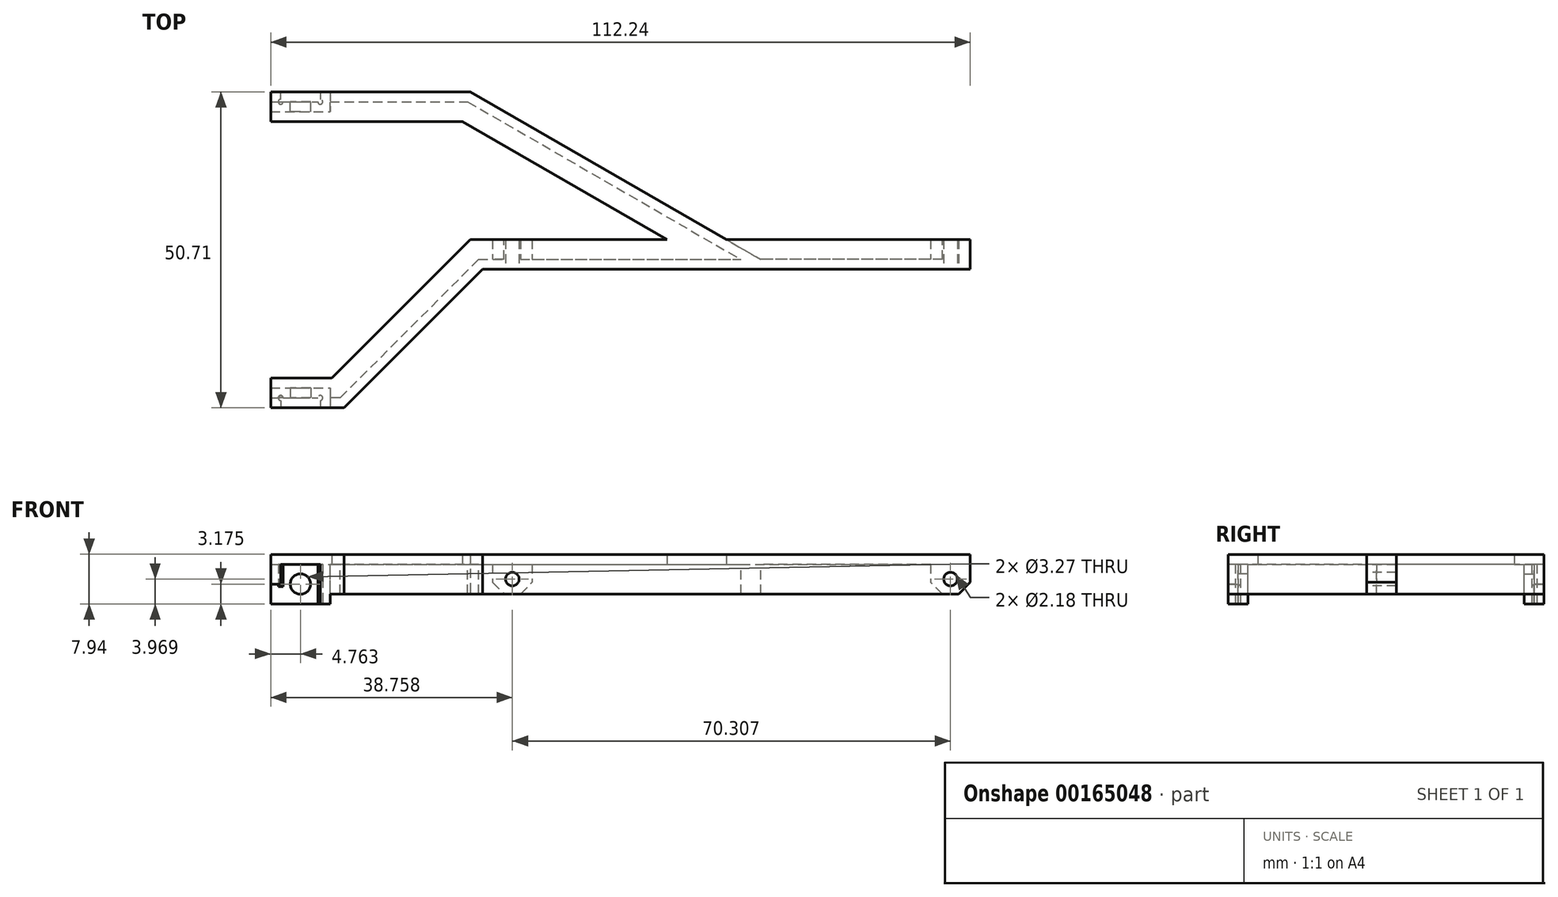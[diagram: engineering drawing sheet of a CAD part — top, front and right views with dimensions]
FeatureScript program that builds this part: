
annotation { "Feature Type Name" : "Feature", "Feature Type Description" : "" }
export const myFeature = defineFeature(function(context is Context, id is Id, definition is map)
    precondition{}
    {
        {
            var Q0;
            Q0=qCreatedBy(makeId("Top.planeOp"),FACE);
            var sketch = newSketch(context, id + "F0", { "sketchPlane" : qUnion([Q0])});
            skLineSegment(sketch, "E0", {"start": v(-127, 22.22) * mm, "end": v(-87.88, 22.22) * mm});
            skLineSegment(sketch, "E1", {"start": v(-46.78, 22.23) * mm, "end": v(-24.56, 0) * mm});
            skLineSegment(sketch, "E2", {"start": v(-24.56, 0) * mm, "end": v(24.56, 0) * mm});
            skLineSegment(sketch, "E3", {"start": v(24.56, 0) * mm, "end": v(46.78, 22.23) * mm});
            skLineSegment(sketch, "E4", {"start": v(87.88, 22.23) * mm, "end": v(127, 22.23) * mm});
            skLineSegment(sketch, "E5", {"start": v(-127, 22.23) * mm, "end": v(-127, 17.46) * mm});
            skLineSegment(sketch, "E6", {"start": v(-127, 17.46) * mm, "end": v(-48.76, 17.46) * mm});
            skLineSegment(sketch, "E7", {"start": v(-48.76, 17.46) * mm, "end": v(-26.53, -4.76) * mm});
            skLineSegment(sketch, "E8", {"start": v(-26.53, -4.76) * mm, "end": v(26.53, -4.76) * mm});
            skLineSegment(sketch, "E9", {"start": v(26.53, -4.76) * mm, "end": v(48.76, 17.46) * mm});
            skLineSegment(sketch, "E10", {"start": v(48.76, 17.46) * mm, "end": v(127, 17.46) * mm});
            skLineSegment(sketch, "E11", {"start": v(127, 17.46) * mm, "end": v(127, 22.23) * mm});
            skLineSegment(sketch, "E12", {"start": v(-35.67, 11.11) * mm, "end": v(-39.04, 7.74) * mm, "construction": true});
            skLineSegment(sketch, "E13", {"start": v(0, 0) * mm, "end": v(0, -4.76) * mm, "construction": true});
            skLineSegment(sketch, "E14", {"start": v(35.67, 11.11) * mm, "end": v(39.04, 7.74) * mm, "construction": true});
            skLineSegment(sketch, "E15", {"start": v(-87.88, 17.46) * mm, "end": v(-87.88, 22.23) * mm, "construction": true});
            skLineSegment(sketch, "E16", {"start": v(87.88, 17.46) * mm, "end": v(87.88, 22.23) * mm, "construction": true});
            skLineSegment(sketch, "E17", {"start": v(-87.88, 22.23) * mm, "end": v(-46.78, 45.95) * mm});
            skLineSegment(sketch, "E18", {"start": v(-78.35, 22.23) * mm, "end": v(-45.5, 41.19) * mm});
            skLineSegment(sketch, "E19", {"start": v(-45.5, 41.19) * mm, "end": v(45.5, 41.19) * mm});
            skLineSegment(sketch, "E20", {"start": v(-46.78, 45.95) * mm, "end": v(46.78, 45.95) * mm});
            skLineSegment(sketch, "E21", {"start": v(-78.35, 22.22) * mm, "end": v(-46.78, 22.22) * mm});
            skLineSegment(sketch, "E22", {"start": v(45.5, 41.19) * mm, "end": v(78.35, 22.22) * mm});
            skLineSegment(sketch, "E23", {"start": v(46.78, 45.95) * mm, "end": v(87.88, 22.22) * mm});
            skLineSegment(sketch, "E24", {"start": v(46.78, 22.23) * mm, "end": v(78.35, 22.23) * mm});
            skLineSegment(sketch, "E25", {"start": v(0, 0) * mm, "end": v(0, 41.19) * mm, "construction": true});
            skLineSegment(sketch, "E26", {"start": v(0, 41.19) * mm, "end": v(0, 45.95) * mm, "construction": true});
            skLineSegment(sketch, "E27", {"start": v(-61.93, 31.7) * mm, "end": v(-64.31, 35.83) * mm, "construction": true});
            skLineSegment(sketch, "E28", {"start": v(61.93, 31.7) * mm, "end": v(64.31, 35.83) * mm, "construction": true});
            skLineSegment(sketch, "E29", {"start": v(-46.78, 22.23) * mm, "end": v(0, 22.23) * mm, "construction": true});
            skLineSegment(sketch, "E30", {"start": v(0, 22.23) * mm, "end": v(46.78, 22.23) * mm, "construction": true});
            skSolve(sketch);
        }
        {
            var Q0;
            Q0=qSketchRegion(id+"F0",true);
            extrude(context, id + "F1", {"entities" : qUnion([Q0]), "depth" : 1.59 * mm});
        }
        {
            var Q0;
            Q0=makeQuery(id+"F1.opExtrude","CAP_FACE",FACE,{"disambiguationData":[OSD([sQuery(id+"F0.wireOp",EDGE,"E0"),sQuery(id+"F0.wireOp",EDGE,"E1"),sQuery(id+"F0.wireOp",EDGE,"E2"),sQuery(id+"F0.wireOp",EDGE,"E3"),sQuery(id+"F0.wireOp",EDGE,"E4"),sQuery(id+"F0.wireOp",EDGE,"E5"),sQuery(id+"F0.wireOp",EDGE,"E6"),sQuery(id+"F0.wireOp",EDGE,"E7"),sQuery(id+"F0.wireOp",EDGE,"E8"),sQuery(id+"F0.wireOp",EDGE,"E9"),sQuery(id+"F0.wireOp",EDGE,"E10"),sQuery(id+"F0.wireOp",EDGE,"E11"),sQuery(id+"F0.wireOp",EDGE,"E17"),sQuery(id+"F0.wireOp",EDGE,"E18"),sQuery(id+"F0.wireOp",EDGE,"E19"),sQuery(id+"F0.wireOp",EDGE,"E20"),sQuery(id+"F0.wireOp",EDGE,"E21"),sQuery(id+"F0.wireOp",EDGE,"E22"),sQuery(id+"F0.wireOp",EDGE,"E23"),sQuery(id+"F0.wireOp",EDGE,"E24")])],"isStart":true});
            var sketch = newSketch(context, id + "F2", { "sketchPlane" : qUnion([Q0])});
            skLineSegment(sketch, "E31.bottom", {"start": v(-127, -17.46) * mm, "end": v(-48.76, -17.46) * mm});
            skLineSegment(sketch, "E31.top", {"start": v(-127, -19.05) * mm, "end": v(-93.38, -19.05) * mm});
            skLineSegment(sketch, "E31.left", {"start": v(-127, -19.05) * mm, "end": v(-127, -17.46) * mm});
            skLineSegment(sketch, "E32", {"start": v(-48.76, -17.46) * mm, "end": v(-26.53, 4.76) * mm});
            skLineSegment(sketch, "E33", {"start": v(-26.53, 4.76) * mm, "end": v(26.53, 4.76) * mm});
            skLineSegment(sketch, "E34", {"start": v(26.53, 4.76) * mm, "end": v(48.76, -17.46) * mm});
            skLineSegment(sketch, "E35", {"start": v(48.76, -17.46) * mm, "end": v(127, -17.46) * mm});
            skLineSegment(sketch, "E36", {"start": v(127, -19.05) * mm, "end": v(127, -17.46) * mm});
            skLineSegment(sketch, "E37", {"start": v(127, -19.05) * mm, "end": v(93.38, -19.05) * mm});
            skLineSegment(sketch, "E38", {"start": v(-25.87, 3.18) * mm, "end": v(-48.1, -19.05) * mm});
            skLineSegment(sketch, "E39", {"start": v(-36.52, -7.47) * mm, "end": v(-37.64, -6.35) * mm, "construction": true});
            skLineSegment(sketch, "E40", {"start": v(36.52, -7.47) * mm, "end": v(37.64, -6.35) * mm, "construction": true});
            skLineSegment(sketch, "E41", {"start": v(0, 4.76) * mm, "end": v(0, 3.17) * mm, "construction": true});
            skLineSegment(sketch, "E42", {"start": v(-25.87, 3.17) * mm, "end": v(-4.29, 3.17) * mm});
            skLineSegment(sketch, "E43.top", {"start": v(-4.29, 1.59) * mm, "end": v(24.29, 1.59) * mm});
            skLineSegment(sketch, "E43.left", {"start": v(-4.29, 1.59) * mm, "end": v(-4.29, 3.18) * mm});
            skLineSegment(sketch, "E43.right", {"start": v(24.29, 1.59) * mm, "end": v(24.29, 3.18) * mm});
            skLineSegment(sketch, "E44", {"start": v(-46.78, -45.95) * mm, "end": v(-93.38, -19.05) * mm});
            skLineSegment(sketch, "E45", {"start": v(-46.78, -45.95) * mm, "end": v(46.78, -45.95) * mm});
            skLineSegment(sketch, "E46", {"start": v(46.78, -45.95) * mm, "end": v(93.38, -19.05) * mm});
            skLineSegment(sketch, "E47", {"start": v(-66.54, -32.71) * mm, "end": v(-67.33, -34.09) * mm, "construction": true});
            skLineSegment(sketch, "E48", {"start": v(0, -44.36) * mm, "end": v(0, -45.95) * mm, "construction": true});
            skLineSegment(sketch, "E49", {"start": v(66.54, -32.71) * mm, "end": v(67.33, -34.09) * mm, "construction": true});
            skLineSegment(sketch, "E50", {"start": v(-90.2, -19.05) * mm, "end": v(-46.36, -44.36) * mm});
            skLineSegment(sketch, "E51", {"start": v(46.36, -44.36) * mm, "end": v(90.2, -19.05) * mm});
            skLineSegment(sketch, "E52", {"start": v(-48.1, -19.05) * mm, "end": v(-90.2, -19.05) * mm});
            skLineSegment(sketch, "E53", {"start": v(48.1, -19.05) * mm, "end": v(90.2, -19.05) * mm});
            skLineSegment(sketch, "E54.bottom", {"start": v(-4.29, -44.36) * mm, "end": v(24.29, -44.36) * mm, "construction": true});
            skLineSegment(sketch, "E54.top", {"start": v(-4.29, -42.78) * mm, "end": v(24.29, -42.78) * mm});
            skLineSegment(sketch, "E54.left", {"start": v(-4.29, -42.78) * mm, "end": v(-4.29, -44.36) * mm});
            skLineSegment(sketch, "E54.right", {"start": v(24.29, -42.78) * mm, "end": v(24.29, -44.36) * mm});
            skLineSegment(sketch, "E55", {"start": v(-4.29, -44.36) * mm, "end": v(-46.36, -44.36) * mm});
            skLineSegment(sketch, "E56", {"start": v(24.29, -44.36) * mm, "end": v(46.36, -44.36) * mm});
            skLineSegment(sketch, "E57", {"start": v(24.29, 3.17) * mm, "end": v(-4.29, 3.17) * mm, "construction": true});
            skLineSegment(sketch, "E58", {"start": v(48.1, -19.05) * mm, "end": v(25.87, 3.18) * mm});
            skLineSegment(sketch, "E59", {"start": v(25.87, 3.18) * mm, "end": v(24.29, 3.18) * mm});
            skSolve(sketch);
        }
        {
            var Q0;
            Q0=makeQuery(id+"F2.imprint","IMPRINT",FACE,{"disambiguationData":[TD([[makeQuery(id+"F2.imprint","IMPRINT",EDGE,{"derivedFrom":sQuery(id+"F2.wireOp",EDGE,"E31.bottom")}),1.0]])]});
            var Q1;
            Q1=makeQuery(id+"F2.imprint","IMPRINT",FACE,{"disambiguationData":[TD([[makeQuery(id+"F2.imprint","IMPRINT",EDGE,{"derivedFrom":sQuery(id+"F2.wireOp",EDGE,"E31.bottom")}),-1.0]])]});
            extrude(context, id + "F3", {"entities" : qUnion([Q0, Q1]), "operationType" : NewBodyOperationType.ADD, "depth" : 4.76 * mm});
        }
        {
            var Q0;
            Q0=makeQuery(id+"F3.opExtrude","SWEPT_FACE",FACE,{"disambiguationData":[OSD([sQuery(id+"F2.wireOp",EDGE,"E31.top")])]});
            var sketch = newSketch(context, id + "F4", { "sketchPlane" : qUnion([Q0])});
            skLineSegment(sketch, "E60.bottom", {"start": v(-50.34, -4.76) * mm, "end": v(-56.7, -4.76) * mm});
            skLineSegment(sketch, "E60.top", {"start": v(-50.34, 1.59) * mm, "end": v(-56.7, 1.59) * mm});
            skLineSegment(sketch, "E60.left", {"start": v(-50.34, 1.59) * mm, "end": v(-50.34, -4.76) * mm});
            skLineSegment(sketch, "E60.right", {"start": v(-56.7, 1.59) * mm, "end": v(-56.7, -4.76) * mm});
            skLineSegment(sketch, "E61", {"start": v(-50.34, -1.59) * mm, "end": v(-48.76, -1.59) * mm, "construction": true});
            skLineSegment(sketch, "E62.bottom", {"start": v(-127, -4.76) * mm, "end": v(-120.65, -4.76) * mm});
            skLineSegment(sketch, "E62.top", {"start": v(-127, 1.59) * mm, "end": v(-120.65, 1.59) * mm});
            skLineSegment(sketch, "E62.left", {"start": v(-127, 1.59) * mm, "end": v(-127, -4.76) * mm});
            skLineSegment(sketch, "E62.right", {"start": v(-120.65, 1.59) * mm, "end": v(-120.65, -4.76) * mm});
            skLineSegment(sketch, "E63.bottom", {"start": v(127, -4.76) * mm, "end": v(122.24, -4.76) * mm});
            skLineSegment(sketch, "E63.top", {"start": v(127, 0) * mm, "end": v(122.24, 0) * mm});
            skLineSegment(sketch, "E63.left", {"start": v(127, 0) * mm, "end": v(127, -4.76) * mm});
            skLineSegment(sketch, "E63.right", {"start": v(122.24, 0) * mm, "end": v(122.24, -4.76) * mm});
            skLineSegment(sketch, "E64.bottom", {"start": v(53.52, -4.76) * mm, "end": v(58.28, -4.76) * mm});
            skLineSegment(sketch, "E64.top", {"start": v(53.52, 0) * mm, "end": v(58.28, 0) * mm});
            skLineSegment(sketch, "E64.left", {"start": v(53.52, 0) * mm, "end": v(53.52, -4.76) * mm});
            skLineSegment(sketch, "E64.right", {"start": v(58.28, 0) * mm, "end": v(58.28, -4.76) * mm});
            skLineSegment(sketch, "E65", {"start": v(122.24, -2.38) * mm, "end": v(58.28, -2.38) * mm, "construction": true});
            skLineSegment(sketch, "E66", {"start": v(-56.7, -1.59) * mm, "end": v(-120.65, -1.59) * mm, "construction": true});
            skSolve(sketch);
        }
        {
            var Q0;
            Q0=qSketchRegion(id+"F4",true);
            var Q1;
            Q1=makeQuery(id+"F1.opExtrude","SWEPT_FACE",FACE,{"disambiguationData":[OSD([sQuery(id+"F0.wireOp",EDGE,"E0")])]});
            extrude(context, id + "F5", {"entities" : qUnion([Q0]), "operationType" : NewBodyOperationType.ADD, "endBound" : BoundingType.UP_TO_SURFACE, "endBoundEntityFace" : qUnion([Q1]), "depth" : 25.4 * mm});
        }
        {
            var Q0;
            Q0=makeQuery(id+"F5.boolean.opBoolean","MERGE",EDGE,{"derivedFrom":[makeQuery(id+"F3.opExtrude","CAP_EDGE",EDGE,{"disambiguationData":[OSD([sQuery(id+"F2.wireOp",EDGE,"E31.left")])],"isStart":false}),makeQuery(id+"F5.opExtrude","SWEPT_EDGE",EDGE,{"disambiguationData":[OSD([sQuery(id+"F4.wireOp",EDGE,"E63.bottom"),sQuery(id+"F4.wireOp",EDGE,"E63.left")])]})]});
            var Q1;
            Q1=makeQuery(id+"F5.opExtrude","SWEPT_EDGE",EDGE,{"disambiguationData":[OSD([sQuery(id+"F2.wireOp",EDGE,"E31.top"),sQuery(id+"F4.wireOp",EDGE,"E63.bottom"),sQuery(id+"F4.wireOp",EDGE,"E63.right")])]});
            var Q2;
            Q2=makeQuery(id+"F5.opExtrude","SWEPT_EDGE",EDGE,{"disambiguationData":[OSD([sQuery(id+"F2.wireOp",EDGE,"E31.top"),sQuery(id+"F4.wireOp",EDGE,"E64.bottom"),sQuery(id+"F4.wireOp",EDGE,"E64.right")])]});
            var Q3;
            Q3=makeQuery(id+"F5.opExtrude","SWEPT_EDGE",EDGE,{"disambiguationData":[OSD([sQuery(id+"F2.wireOp",EDGE,"E31.top"),sQuery(id+"F4.wireOp",EDGE,"E64.bottom"),sQuery(id+"F4.wireOp",EDGE,"E64.left")])]});
            var Q4;
            Q4=makeQuery(id+"F5.opExtrude","SWEPT_EDGE",EDGE,{"disambiguationData":[OSD([sQuery(id+"F4.wireOp",EDGE,"E60.bottom"),sQuery(id+"F4.wireOp",EDGE,"E60.left")])]});
            var Q5;
            Q5=makeQuery(id+"F5.opExtrude","SWEPT_EDGE",EDGE,{"disambiguationData":[OSD([sQuery(id+"F4.wireOp",EDGE,"E60.bottom"),sQuery(id+"F4.wireOp",EDGE,"E60.right")])]});
            var Q6;
            Q6=makeQuery(id+"F5.opExtrude","SWEPT_EDGE",EDGE,{"disambiguationData":[OSD([sQuery(id+"F4.wireOp",EDGE,"E62.bottom"),sQuery(id+"F4.wireOp",EDGE,"E62.right")])]});
            var Q7;
            Q7=makeQuery(id+"F5.boolean.opBoolean","MERGE",EDGE,{"derivedFrom":[makeQuery(id+"F3.opExtrude","CAP_EDGE",EDGE,{"disambiguationData":[OSD([sQuery(id+"F2.wireOp",EDGE,"E36")])],"isStart":false}),makeQuery(id+"F5.opExtrude","SWEPT_EDGE",EDGE,{"disambiguationData":[OSD([sQuery(id+"F4.wireOp",EDGE,"E62.bottom"),sQuery(id+"F4.wireOp",EDGE,"E62.left")])]})]});
            chamfer(context, id + "F6", {"entities" : qUnion([Q0, Q1, Q2, Q3, Q4, Q5, Q6, Q7]), "width" : 1.86 * mm, "tangentPropagation" : true});
        }
        {
            var Q0;
            Q0=makeQuery(id+"F5.boolean.opBoolean","MERGE",FACE,{"derivedFrom":[makeQuery(id+"F3.opExtrude","CAP_FACE",FACE,{"disambiguationData":[OSD([sQuery(id+"F2.wireOp",EDGE,"E31.bottom"),sQuery(id+"F2.wireOp",EDGE,"E31.top"),sQuery(id+"F2.wireOp",EDGE,"E31.left"),sQuery(id+"F2.wireOp",EDGE,"E32"),sQuery(id+"F2.wireOp",EDGE,"E33"),sQuery(id+"F2.wireOp",EDGE,"E34"),sQuery(id+"F2.wireOp",EDGE,"E35"),sQuery(id+"F2.wireOp",EDGE,"E36"),sQuery(id+"F2.wireOp",EDGE,"E37"),sQuery(id+"F2.wireOp",EDGE,"XaXFcP98-jHVc-UIB6-hOLf-KzhYTJMkncuN"),sQuery(id+"F2.wireOp",EDGE,"E38"),sQuery(id+"F2.wireOp",EDGE,"E42"),sQuery(id+"F2.wireOp",EDGE,"r7zNDvTV-qKGN-hqvY-1zE9-Y1A1LRN73BV9"),sQuery(id+"F2.wireOp",EDGE,"E43.top"),sQuery(id+"F2.wireOp",EDGE,"E43.left"),sQuery(id+"F2.wireOp",EDGE,"E43.right")])],"isStart":false}),makeQuery(id+"F5.opExtrude","SWEPT_FACE",FACE,{"disambiguationData":[OSD([sQuery(id+"F4.wireOp",EDGE,"E60.bottom")])]}),makeQuery(id+"F5.opExtrude","SWEPT_FACE",FACE,{"disambiguationData":[OSD([sQuery(id+"F4.wireOp",EDGE,"E62.bottom")])]}),makeQuery(id+"F5.opExtrude","SWEPT_FACE",FACE,{"disambiguationData":[OSD([sQuery(id+"F4.wireOp",EDGE,"E63.bottom")])]}),makeQuery(id+"F5.opExtrude","SWEPT_FACE",FACE,{"disambiguationData":[OSD([sQuery(id+"F4.wireOp",EDGE,"E64.bottom")])]})]});
            var sketch = newSketch(context, id + "F7", { "sketchPlane" : qUnion([Q0])});
            skLineSegment(sketch, "E67.bottom", {"start": v(-4.29, 1.59) * mm, "end": v(24.29, 1.59) * mm});
            skLineSegment(sketch, "E67.top", {"start": v(-4.29, 4.76) * mm, "end": v(24.29, 4.76) * mm});
            skLineSegment(sketch, "E67.left", {"start": v(-4.29, 4.76) * mm, "end": v(-4.29, 1.59) * mm});
            skLineSegment(sketch, "E67.right", {"start": v(24.29, 4.76) * mm, "end": v(24.29, 1.59) * mm});
            skLineSegment(sketch, "E68.bottom", {"start": v(-4.29, -42.78) * mm, "end": v(24.29, -42.78) * mm});
            skLineSegment(sketch, "E68.top", {"start": v(-4.29, -45.95) * mm, "end": v(24.29, -45.95) * mm});
            skLineSegment(sketch, "E68.left", {"start": v(-4.29, -45.95) * mm, "end": v(-4.29, -42.78) * mm});
            skLineSegment(sketch, "E68.right", {"start": v(24.29, -45.95) * mm, "end": v(24.29, -42.78) * mm});
            skSolve(sketch);
        }
        {
            var Q0;
            Q0=qSketchRegion(id+"F7",true);
            extrude(context, id + "F8", {"entities" : qUnion([Q0]), "operationType" : NewBodyOperationType.ADD, "depth" : 1.59 * mm});
        }
        {
            var Q0;
            Q0=makeQuery(id+"F8.opExtrude","CAP_FACE",FACE,{"disambiguationData":[OSD([sQuery(id+"F7.wireOp",EDGE,"E68.bottom"),sQuery(id+"F7.wireOp",EDGE,"E68.top"),sQuery(id+"F7.wireOp",EDGE,"E68.left"),sQuery(id+"F7.wireOp",EDGE,"E68.right")])],"isStart":false});
            var sketch = newSketch(context, id + "F9", { "sketchPlane" : qUnion([Q0])});
            skLineSegment(sketch, "E69.bottom", {"start": v(16.35, 4.76) * mm, "end": v(22.7, 4.76) * mm});
            skLineSegment(sketch, "E69.top", {"start": v(16.35, 3.17) * mm, "end": v(22.7, 3.17) * mm});
            skLineSegment(sketch, "E69.left", {"start": v(16.35, 3.17) * mm, "end": v(16.35, 4.76) * mm});
            skLineSegment(sketch, "E69.right", {"start": v(22.7, 3.17) * mm, "end": v(22.7, 4.76) * mm});
            skLineSegment(sketch, "E70.bottom", {"start": v(22.7, 3.17) * mm, "end": v(24.29, 3.17) * mm, "construction": true});
            skLineSegment(sketch, "E70.top", {"start": v(22.7, 1.59) * mm, "end": v(24.29, 1.59) * mm, "construction": true});
            skLineSegment(sketch, "E70.left", {"start": v(22.7, 1.59) * mm, "end": v(22.7, 3.17) * mm, "construction": true});
            skLineSegment(sketch, "E70.right", {"start": v(24.29, 1.59) * mm, "end": v(24.29, 3.17) * mm, "construction": true});
            skLineSegment(sketch, "E71.bottom", {"start": v(24.29, -44.36) * mm, "end": v(22.7, -44.36) * mm, "construction": true});
            skLineSegment(sketch, "E71.top", {"start": v(24.29, -42.78) * mm, "end": v(22.7, -42.78) * mm, "construction": true});
            skLineSegment(sketch, "E71.left", {"start": v(24.29, -42.78) * mm, "end": v(24.29, -44.36) * mm, "construction": true});
            skLineSegment(sketch, "E71.right", {"start": v(22.7, -42.78) * mm, "end": v(22.7, -44.36) * mm, "construction": true});
            skLineSegment(sketch, "E72.bottom", {"start": v(16.35, -44.36) * mm, "end": v(22.7, -44.36) * mm});
            skLineSegment(sketch, "E72.top", {"start": v(16.35, -45.95) * mm, "end": v(22.7, -45.95) * mm});
            skLineSegment(sketch, "E72.left", {"start": v(16.35, -45.95) * mm, "end": v(16.35, -44.36) * mm});
            skLineSegment(sketch, "E72.right", {"start": v(22.7, -45.95) * mm, "end": v(22.7, -44.36) * mm});
            skSolve(sketch);
        }
        {
            var Q0;
            Q0=qSketchRegion(id+"F9",true);
            var Q1;
            {var subQ2=sQuery(id+"F0.wireOp",EDGE,"E21");var subQ7=sQuery(id+"F0.wireOp",EDGE,"E24");var subQ10=sQuery(id+"F0.wireOp",EDGE,"E1");var subQ11=makeQuery(id+"F1.opExtrude","SWEPT_FACE",FACE,{"disambiguationData":[OSD([subQ10])]});var subQ14=sQuery(id+"F0.wireOp",EDGE,"E2");var subQ17=sQuery(id+"F0.wireOp",EDGE,"E3");var subQ19=sQuery(id+"F0.wireOp",EDGE,"E0");var subQ22=sQuery(id+"F0.wireOp",EDGE,"E18");var subQ23=sQuery(id+"F0.wireOp",EDGE,"E19");var subQ24=sQuery(id+"F0.wireOp",EDGE,"E22");Q1=makeQuery(id+"F5.boolean.opBoolean","SPLIT",FACE,{"disambiguationData":[TD([subQ11])],"derivedFrom":makeQuery(id+"F3.boolean.opBoolean","SPLIT",FACE,{"disambiguationData":[TD([subQ11])],"derivedFrom":makeQuery(id+"F1.opExtrude","CAP_FACE",FACE,{"disambiguationData":[OSD([subQ19,subQ10,subQ14,subQ17,sQuery(id+"F0.wireOp",EDGE,"E4"),sQuery(id+"F0.wireOp",EDGE,"E5"),sQuery(id+"F0.wireOp",EDGE,"E6"),sQuery(id+"F0.wireOp",EDGE,"E7"),sQuery(id+"F0.wireOp",EDGE,"E8"),sQuery(id+"F0.wireOp",EDGE,"E9"),sQuery(id+"F0.wireOp",EDGE,"E10"),sQuery(id+"F0.wireOp",EDGE,"E11"),sQuery(id+"F0.wireOp",EDGE,"E17"),subQ22,subQ23,sQuery(id+"F0.wireOp",EDGE,"E20"),subQ2,subQ24,sQuery(id+"F0.wireOp",EDGE,"E23"),subQ7])],"isStart":true})})});}
            extrude(context, id + "F10", {"entities" : qUnion([Q0]), "operationType" : NewBodyOperationType.REMOVE, "endBound" : BoundingType.UP_TO_SURFACE, "oppositeDirection" : true, "endBoundEntityFace" : qUnion([Q1]), "depth" : 25.4 * mm});
        }
        {
            var Q0;
            Q0=makeQuery(id+"F10.boolean.opBoolean","COPY",FACE,{"derivedFrom":makeQuery(id+"F10.opExtrude","SWEPT_FACE",FACE,{"disambiguationData":[OSD([sQuery(id+"F9.wireOp",EDGE,"E69.top")])]})});
            var sketch = newSketch(context, id + "F11", { "sketchPlane" : qUnion([Q0])});
            skLineSegment(sketch, "E73", {"start": v(123.83, 0) * mm, "end": v(123.83, -4.76) * mm, "construction": true});
            skLineSegment(sketch, "E74", {"start": v(53.52, 0) * mm, "end": v(53.52, -4.76) * mm, "construction": true});
            skCircle(sketch, "E75", {"center": v(53.52, -2.38) * mm, "radius": 1.1 * mm});
            skCircle(sketch, "E76", {"center": v(123.83, -2.38) * mm, "radius": 1.1 * mm});
            skLineSegment(sketch, "E77", {"start": v(-55.9, 0) * mm, "end": v(-55.9, -4.76) * mm, "construction": true});
            skLineSegment(sketch, "E78", {"start": v(-124.62, 0) * mm, "end": v(-124.62, -4.76) * mm, "construction": true});
            skCircle(sketch, "E79", {"center": v(-124.62, -2.38) * mm, "radius": 1.1 * mm});
            skCircle(sketch, "E80", {"center": v(-55.9, -2.38) * mm, "radius": 1.1 * mm});
            skLineSegment(sketch, "E81", {"start": v(19.52, -3.17) * mm, "end": v(19.52, -6.35) * mm, "construction": true});
            skCircle(sketch, "E82", {"center": v(19.52, -3.17) * mm, "radius": 1.63 * mm});
            skSolve(sketch);
        }
        {
            var Q0;
            Q0=qSketchRegion(id+"F11",true);
            var Q1;
            Q1=makeQuery(id+"F5.boolean.opBoolean","MERGE",FACE,{"derivedFrom":[makeQuery(id+"F1.opExtrude","SWEPT_FACE",FACE,{"disambiguationData":[OSD([sQuery(id+"F0.wireOp",EDGE,"E21")])]}),makeQuery(id+"F5.opExtrude","CAP_FACE",FACE,{"disambiguationData":[OSD([sQuery(id+"F0.wireOp",EDGE,"E0")]),ownerDisambiguation([makeQuery(id+"F5.opExtrude","SWEPT_BODY",BODY,{"disambiguationData":[OSD([sQuery(id+"F4.wireOp",EDGE,"E64.bottom"),sQuery(id+"F4.wireOp",EDGE,"E64.top"),sQuery(id+"F4.wireOp",EDGE,"E64.left"),sQuery(id+"F4.wireOp",EDGE,"E64.right")])]})])],"isStart":false})]});
            extrude(context, id + "F12", {"entities" : qUnion([Q0]), "operationType" : NewBodyOperationType.REMOVE, "endBound" : BoundingType.UP_TO_SURFACE, "oppositeDirection" : true, "endBoundEntityFace" : qUnion([Q1]), "depth" : 25.4 * mm});
        }
        {
            var Q0;
            Q0=makeQuery(id+"F8.opExtrude","CAP_EDGE",EDGE,{"disambiguationData":[OSD([sQuery(id+"F7.wireOp",EDGE,"E67.left")])],"isStart":true});
            var Q1;
            Q1=makeQuery(id+"F8.opExtrude","CAP_EDGE",EDGE,{"disambiguationData":[OSD([sQuery(id+"F7.wireOp",EDGE,"E67.right")])],"isStart":true});
            var Q2;
            Q2=makeQuery(id+"F8.opExtrude","CAP_EDGE",EDGE,{"disambiguationData":[OSD([sQuery(id+"F7.wireOp",EDGE,"E68.left")])],"isStart":true});
            var Q3;
            Q3=makeQuery(id+"F8.opExtrude","CAP_EDGE",EDGE,{"disambiguationData":[OSD([sQuery(id+"F7.wireOp",EDGE,"E68.right")])],"isStart":true});
            chamfer(context, id + "F13", {"entities" : qUnion([Q0, Q1, Q2, Q3]), "width" : 1.59 * mm, "tangentPropagation" : true});
        }
        {
            var Q0;
            Q0=makeQuery(id+"F8.opExtrude","CAP_FACE",FACE,{"disambiguationData":[OSD([sQuery(id+"F7.wireOp",EDGE,"E68.bottom"),sQuery(id+"F7.wireOp",EDGE,"E68.top"),sQuery(id+"F7.wireOp",EDGE,"E68.left"),sQuery(id+"F7.wireOp",EDGE,"E68.right")])],"isStart":false});
            var sketch = newSketch(context, id + "F14", { "sketchPlane" : qUnion([Q0])});
            skCircle(sketch, "E83", {"center": v(22.7, 3.17) * mm, "radius": 0.4 * mm});
            skCircle(sketch, "E84", {"center": v(22.7, -44.36) * mm, "radius": 0.4 * mm});
            skSolve(sketch);
        }
        {
            var Q0;
            Q0=qSketchRegion(id+"F14",true);
            var Q1;
            Q1=makeQuery(id+"F10.boolean.opBoolean","COPY",FACE,{"derivedFrom":makeQuery(id+"F10.opExtrude","CAP_FACE",FACE,{"disambiguationData":[OSD([sQuery(id+"F9.wireOp",EDGE,"E69.bottom"),sQuery(id+"F9.wireOp",EDGE,"E69.top"),sQuery(id+"F9.wireOp",EDGE,"E69.left"),sQuery(id+"F9.wireOp",EDGE,"E69.right")])],"isStart":false})});
            extrude(context, id + "F15", {"entities" : qUnion([Q0]), "operationType" : NewBodyOperationType.REMOVE, "endBound" : BoundingType.UP_TO_SURFACE, "oppositeDirection" : true, "endBoundEntityFace" : qUnion([Q1]), "depth" : 25.4 * mm});
        }
        {
            var Q0;
            Q0=makeQuery(id+"F10.boolean.opBoolean","COPY",FACE,{"derivedFrom":makeQuery(id+"F10.opExtrude","SWEPT_FACE",FACE,{"disambiguationData":[OSD([sQuery(id+"F9.wireOp",EDGE,"E72.bottom")])]})});
            var sketch = newSketch(context, id + "F16", { "sketchPlane" : qUnion([Q0])});
            skCircle(sketch, "E85", {"center": v(-19.52, -3.18) * mm, "radius": 1.63 * mm});
            skSolve(sketch);
        }
        {
            var Q0;
            Q0=makeQuery(id+"F16.imprint","IMPRINT",FACE,{"disambiguationData":[TD([[makeQuery(id+"F16.imprint","IMPRINT",EDGE,{"derivedFrom":sQuery(id+"F16.wireOp",EDGE,"E85")}),1.0]])]});
            var Q1;
            Q1=makeQuery(id+"F8.boolean.opBoolean","MERGE",FACE,{"derivedFrom":[makeQuery(id+"F3.opExtrude","SWEPT_FACE",FACE,{"disambiguationData":[OSD([sQuery(id+"F2.wireOp",EDGE,"E54.top")])]}),makeQuery(id+"F8.opExtrude","SWEPT_FACE",FACE,{"disambiguationData":[OSD([sQuery(id+"F7.wireOp",EDGE,"E68.bottom")])]})]});
            extrude(context, id + "F17", {"entities" : qUnion([Q0]), "operationType" : NewBodyOperationType.REMOVE, "endBound" : BoundingType.UP_TO_SURFACE, "oppositeDirection" : true, "endBoundEntityFace" : qUnion([Q1]), "depth" : 25.4 * mm});
        }
        {
            var Q0;
            Q0=makeQuery(id+"F8.opExtrude","CAP_FACE",FACE,{"disambiguationData":[OSD([sQuery(id+"F7.wireOp",EDGE,"E67.bottom"),sQuery(id+"F7.wireOp",EDGE,"E67.top"),sQuery(id+"F7.wireOp",EDGE,"E67.left"),sQuery(id+"F7.wireOp",EDGE,"E67.right")])],"isStart":false});
            var sketch = newSketch(context, id + "F18", { "sketchPlane" : qUnion([Q0])});
            skLineSegment(sketch, "E86.bottom", {"start": v(14.76, 4.76) * mm, "end": v(-127, 4.76) * mm});
            skLineSegment(sketch, "E86.top", {"start": v(14.76, -45.95) * mm, "end": v(-127, -45.95) * mm});
            skLineSegment(sketch, "E86.left", {"start": v(14.76, -45.95) * mm, "end": v(14.76, 4.76) * mm});
            skLineSegment(sketch, "E86.right", {"start": v(-127, -45.95) * mm, "end": v(-127, 4.76) * mm});
            skLineSegment(sketch, "E87", {"start": v(16.35, -45.16) * mm, "end": v(14.76, -45.16) * mm, "construction": true});
            skSolve(sketch);
        }
        {
            var Q0;
            Q0 = qSketchRegion(id + "F18", true);
            var Q1;
            Q1=makeQuery(id+"F1.opExtrude","CAP_FACE",FACE,{"disambiguationData":[OSD([sQuery(id+"F0.wireOp",EDGE,"E0"),sQuery(id+"F0.wireOp",EDGE,"E1"),sQuery(id+"F0.wireOp",EDGE,"E2"),sQuery(id+"F0.wireOp",EDGE,"E3"),sQuery(id+"F0.wireOp",EDGE,"E4"),sQuery(id+"F0.wireOp",EDGE,"E5"),sQuery(id+"F0.wireOp",EDGE,"E6"),sQuery(id+"F0.wireOp",EDGE,"E7"),sQuery(id+"F0.wireOp",EDGE,"E8"),sQuery(id+"F0.wireOp",EDGE,"E9"),sQuery(id+"F0.wireOp",EDGE,"E10"),sQuery(id+"F0.wireOp",EDGE,"E11"),sQuery(id+"F0.wireOp",EDGE,"E17"),sQuery(id+"F0.wireOp",EDGE,"E18"),sQuery(id+"F0.wireOp",EDGE,"E19"),sQuery(id+"F0.wireOp",EDGE,"E20"),sQuery(id+"F0.wireOp",EDGE,"E21"),sQuery(id+"F0.wireOp",EDGE,"E22"),sQuery(id+"F0.wireOp",EDGE,"E23"),sQuery(id+"F0.wireOp",EDGE,"E24")])],"isStart":false});
            extrude(context, id + "F19", {"entities" : qUnion([Q0]), "operationType" : NewBodyOperationType.REMOVE, "endBound" : BoundingType.UP_TO_SURFACE, "oppositeDirection" : true, "endBoundEntityFace" : qUnion([Q1]), "depth" : 25.4 * mm});
        }
        {
            var Q0;
            Q0=makeQuery(id+"F10.boolean.opBoolean","COPY",FACE,{"derivedFrom":makeQuery(id+"F10.opExtrude","SWEPT_FACE",FACE,{"disambiguationData":[OSD([sQuery(id+"F9.wireOp",EDGE,"E72.left")])]})});
            var sketch = newSketch(context, id + "F20", { "sketchPlane" : qUnion([Q0])});
            skLineSegment(sketch, "E88.bottom", {"start": v(-3.17, -6.35) * mm, "end": v(-4.76, -6.35) * mm});
            skLineSegment(sketch, "E88.top", {"start": v(-3.17, -3.17) * mm, "end": v(-4.76, -3.17) * mm});
            skLineSegment(sketch, "E88.left", {"start": v(-3.17, -3.17) * mm, "end": v(-3.17, -6.35) * mm});
            skLineSegment(sketch, "E88.right", {"start": v(-4.76, -3.17) * mm, "end": v(-4.76, -6.35) * mm});
            skLineSegment(sketch, "E89.bottom", {"start": v(44.36, -6.35) * mm, "end": v(45.95, -6.35) * mm});
            skLineSegment(sketch, "E89.top", {"start": v(44.36, -3.17) * mm, "end": v(45.95, -3.17) * mm});
            skLineSegment(sketch, "E89.left", {"start": v(44.36, -3.17) * mm, "end": v(44.36, -6.35) * mm});
            skLineSegment(sketch, "E89.right", {"start": v(45.95, -3.17) * mm, "end": v(45.95, -6.35) * mm});
            skSolve(sketch);
        }
        {
            var Q0;
            Q0 = qSketchRegion(id + "F20", true);
            var Q1;
            {var subQ5=sQuery(id+"F0.wireOp",EDGE,"E19");Q1=makeQuery(id+"F19.boolean.opBoolean","COPY",FACE,{"disambiguationData":[TD([makeQuery(id+"F1.opExtrude","SWEPT_FACE",FACE,{"disambiguationData":[OSD([subQ5])]})])],"derivedFrom":makeQuery(id+"F19.opExtrude","SWEPT_FACE",FACE,{"disambiguationData":[OSD([sQuery(id+"F18.wireOp",EDGE,"E86.left")])]})});}
            extrude(context, id + "F21", {"entities" : qUnion([Q0]), "operationType" : NewBodyOperationType.REMOVE, "endBound" : BoundingType.UP_TO_SURFACE, "oppositeDirection" : true, "endBoundEntityFace" : qUnion([Q1]), "depth" : 25.4 * mm});
        }
        {
            var Q0;
            Q0=makeQuery(id+"F21.boolean.opBoolean","COPY",FACE,{"derivedFrom":makeQuery(id+"F21.opExtrude","SWEPT_FACE",FACE,{"disambiguationData":[OSD([sQuery(id+"F20.wireOp",EDGE,"E88.top")])]})});
            var sketch = newSketch(context, id + "F22", { "sketchPlane" : qUnion([Q0])});
            skCircle(sketch, "E90", {"center": v(16.35, -44.36) * mm, "radius": 0.4 * mm});
            skCircle(sketch, "E91", {"center": v(16.35, 3.18) * mm, "radius": 0.4 * mm});
            skSolve(sketch);
        }
        {
            var Q0;
            Q0 = qSketchRegion(id + "F22", true);
            var Q1;
            {var subQ0=sQuery(id+"F9.wireOp",EDGE,"E69.right");var subQ1=sQuery(id+"F9.wireOp",EDGE,"E69.left");var subQ2=sQuery(id+"F9.wireOp",EDGE,"E69.top");var subQ3=sQuery(id+"F9.wireOp",EDGE,"E69.bottom");Q1=makeQuery(id+"F15.boolean.opBoolean","MERGE",FACE,{"derivedFrom":[makeQuery(id+"F10.boolean.opBoolean","COPY",FACE,{"derivedFrom":makeQuery(id+"F10.opExtrude","CAP_FACE",FACE,{"disambiguationData":[OSD([subQ3,subQ2,subQ1,subQ0])],"isStart":false})}),makeQuery(id+"F15.opExtrude","CAP_FACE",FACE,{"disambiguationData":[OSD([subQ3,subQ2,subQ1,subQ0]),ownerDisambiguation([makeQuery(id+"F15.opExtrude","SWEPT_BODY",BODY,{"disambiguationData":[OSD([sQuery(id+"F14.wireOp",EDGE,"E83")])]})])],"isStart":false})]});}
            extrude(context, id + "F23", {"entities" : qUnion([Q0]), "operationType" : NewBodyOperationType.REMOVE, "endBound" : BoundingType.UP_TO_SURFACE, "oppositeDirection" : true, "endBoundEntityFace" : qUnion([Q1]), "depth" : 25.4 * mm});
        }
        {
            var Q0;
            Q0=makeQuery(id+"F23.boolean.opBoolean","INTERSECT",EDGE,{"derivedFrom":[makeQuery(id+"F21.boolean.opBoolean","MERGE",FACE,{"derivedFrom":[makeQuery(id+"F10.boolean.opBoolean","COPY",FACE,{"derivedFrom":makeQuery(id+"F10.opExtrude","SWEPT_FACE",FACE,{"disambiguationData":[OSD([sQuery(id+"F9.wireOp",EDGE,"E69.top")])]})})],"fromTools":[makeQuery(id+"F21.opExtrude","SWEPT_FACE",FACE,{"disambiguationData":[OSD([sQuery(id+"F20.wireOp",EDGE,"E88.left")])]})]}),makeQuery(id+"F23.opExtrude","CAP_FACE",FACE,{"disambiguationData":[OSD([sQuery(id+"F22.wireOp",EDGE,"E91")])],"isStart":true})]});
            var Q1;
            Q1=makeQuery(id+"F23.boolean.opBoolean","INTERSECT",EDGE,{"derivedFrom":[makeQuery(id+"F21.boolean.opBoolean","MERGE",FACE,{"derivedFrom":[makeQuery(id+"F10.boolean.opBoolean","COPY",FACE,{"derivedFrom":makeQuery(id+"F10.opExtrude","SWEPT_FACE",FACE,{"disambiguationData":[OSD([sQuery(id+"F9.wireOp",EDGE,"E72.bottom")])]})})],"fromTools":[makeQuery(id+"F21.opExtrude","SWEPT_FACE",FACE,{"disambiguationData":[OSD([sQuery(id+"F20.wireOp",EDGE,"E89.left")])]})]}),makeQuery(id+"F23.opExtrude","CAP_FACE",FACE,{"disambiguationData":[OSD([sQuery(id+"F22.wireOp",EDGE,"E90")])],"isStart":true})]});
            chamfer(context, id + "F24", {"entities" : qUnion([Q0, Q1]), "width" : 0.4 * mm, "tangentPropagation" : true});
        }
    });
